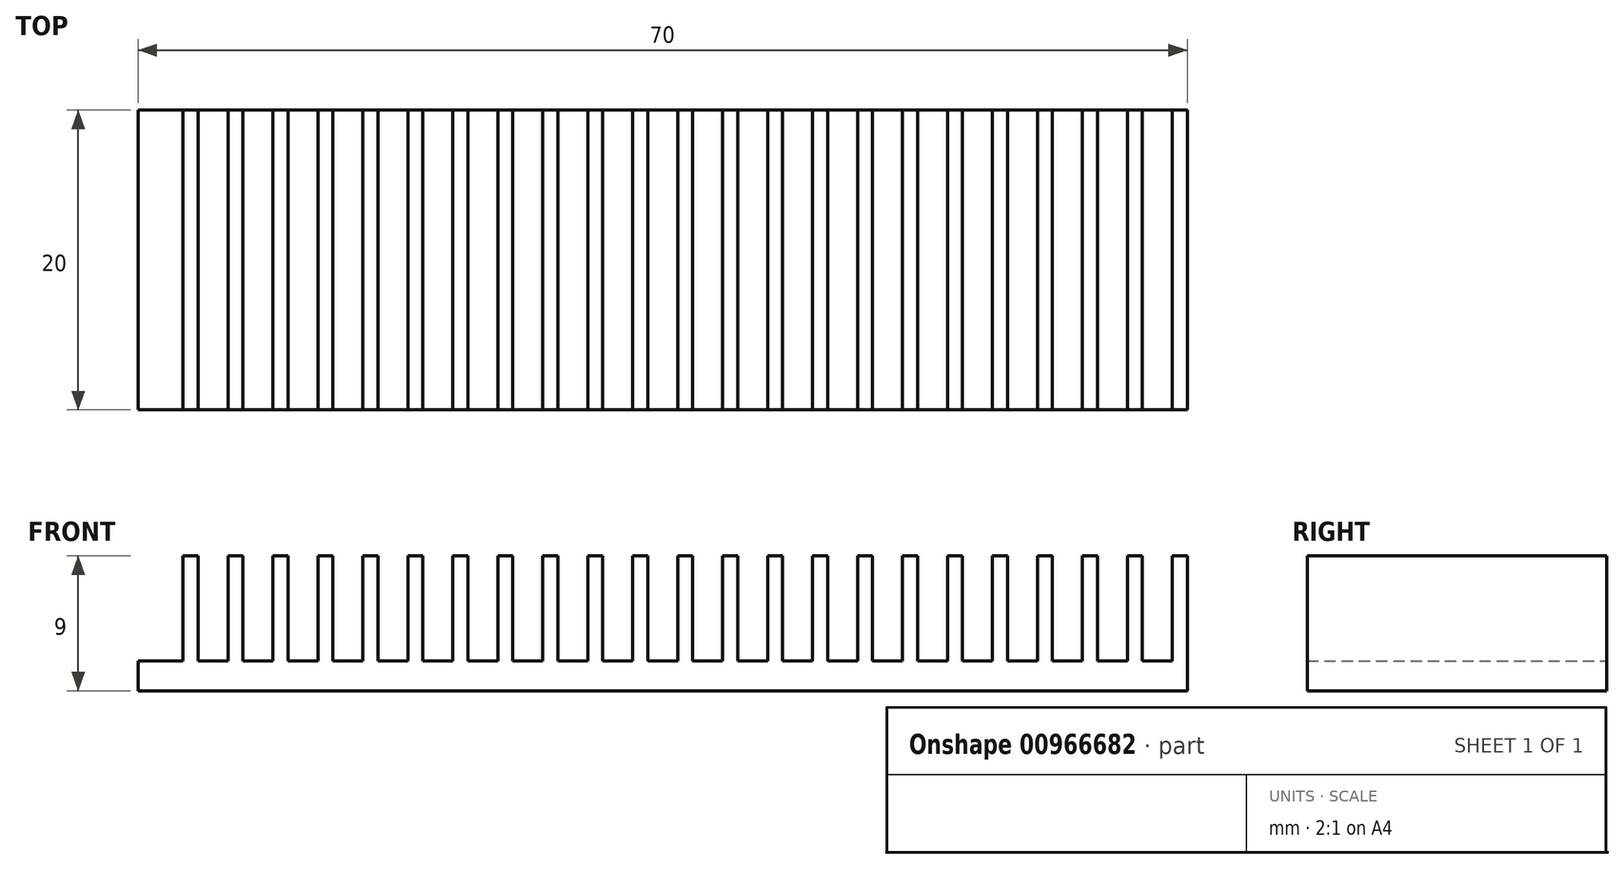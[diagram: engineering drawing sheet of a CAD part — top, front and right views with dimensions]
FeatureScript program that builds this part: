
annotation { "Feature Type Name" : "Feature", "Feature Type Description" : "" }
export const myFeature = defineFeature(function(context is Context, id is Id, definition is map)
    precondition{}
    {
        {
            var Q0;
            Q0=qCreatedBy(makeId("Front.planeOp"),FACE);
            var sketch = newSketch(context, id + "F0", { "sketchPlane" : qUnion([Q0])});
            skLineSegment(sketch, "E0.bottom", {"start": v(-37.94, 0) * mm, "end": v(32.06, 0) * mm});
            skLineSegment(sketch, "E0.top", {"start": v(-37.94, 2) * mm, "end": v(32.06, 2) * mm});
            skLineSegment(sketch, "E0.left", {"start": v(-37.94, 0) * mm, "end": v(-37.94, 2) * mm});
            skLineSegment(sketch, "E0.right", {"start": v(32.06, 0) * mm, "end": v(32.06, 2) * mm});
            skLineSegment(sketch, "E1.bottom", {"start": v(-37.94, 2) * mm, "end": v(-36.94, 2) * mm});
            skLineSegment(sketch, "E1.top", {"start": v(-37.94, 9) * mm, "end": v(-36.94, 9) * mm});
            skLineSegment(sketch, "E1.left", {"start": v(-37.94, 2) * mm, "end": v(-37.94, 9) * mm});
            skLineSegment(sketch, "E1.right", {"start": v(-36.94, 2) * mm, "end": v(-36.94, 9) * mm});
            skLineSegment(sketch, "E2.1.0.0", {"start": v(-34.94, 2) * mm, "end": v(-34.94, 9) * mm});
            skLineSegment(sketch, "E2.1.0.1", {"start": v(-34.94, 9) * mm, "end": v(-33.94, 9) * mm});
            skLineSegment(sketch, "E2.1.0.2", {"start": v(-33.94, 2) * mm, "end": v(-33.94, 9) * mm});
            skLineSegment(sketch, "E2.2.0.0", {"start": v(-31.94, 2) * mm, "end": v(-31.94, 9) * mm});
            skLineSegment(sketch, "E2.2.0.1", {"start": v(-31.94, 9) * mm, "end": v(-30.94, 9) * mm});
            skLineSegment(sketch, "E2.2.0.2", {"start": v(-30.94, 2) * mm, "end": v(-30.94, 9) * mm});
            skLineSegment(sketch, "E2.3.0.0", {"start": v(-28.94, 2) * mm, "end": v(-28.94, 9) * mm});
            skLineSegment(sketch, "E2.3.0.1", {"start": v(-28.94, 9) * mm, "end": v(-27.94, 9) * mm});
            skLineSegment(sketch, "E2.3.0.2", {"start": v(-27.94, 2) * mm, "end": v(-27.94, 9) * mm});
            skLineSegment(sketch, "E2.4.0.0", {"start": v(-25.94, 2) * mm, "end": v(-25.94, 9) * mm});
            skLineSegment(sketch, "E2.4.0.1", {"start": v(-25.94, 9) * mm, "end": v(-24.94, 9) * mm});
            skLineSegment(sketch, "E2.4.0.2", {"start": v(-24.94, 2) * mm, "end": v(-24.94, 9) * mm});
            skLineSegment(sketch, "E2.5.0.0", {"start": v(-22.94, 2) * mm, "end": v(-22.94, 9) * mm});
            skLineSegment(sketch, "E2.5.0.1", {"start": v(-22.94, 9) * mm, "end": v(-21.94, 9) * mm});
            skLineSegment(sketch, "E2.5.0.2", {"start": v(-21.94, 2) * mm, "end": v(-21.94, 9) * mm});
            skLineSegment(sketch, "E2.6.0.0", {"start": v(-19.94, 2) * mm, "end": v(-19.94, 9) * mm});
            skLineSegment(sketch, "E2.6.0.1", {"start": v(-19.94, 9) * mm, "end": v(-18.94, 9) * mm});
            skLineSegment(sketch, "E2.6.0.2", {"start": v(-18.94, 2) * mm, "end": v(-18.94, 9) * mm});
            skLineSegment(sketch, "E2.7.0.0", {"start": v(-16.94, 2) * mm, "end": v(-16.94, 9) * mm});
            skLineSegment(sketch, "E2.7.0.1", {"start": v(-16.94, 9) * mm, "end": v(-15.94, 9) * mm});
            skLineSegment(sketch, "E2.7.0.2", {"start": v(-15.94, 2) * mm, "end": v(-15.94, 9) * mm});
            skLineSegment(sketch, "E2.direction1", {"start": v(-37.94, 2) * mm, "end": v(-34.94, 2) * mm, "construction": true});
            skLineSegment(sketch, "E3.0.8.0", {"start": v(-13.94, 2) * mm, "end": v(-13.94, 9) * mm});
            skLineSegment(sketch, "E3.3.8.0", {"start": v(-13.94, 9) * mm, "end": v(-12.94, 9) * mm});
            skLineSegment(sketch, "E3.6.8.0", {"start": v(-12.94, 2) * mm, "end": v(-12.94, 9) * mm});
            skLineSegment(sketch, "E3.0.9.0", {"start": v(-10.94, 2) * mm, "end": v(-10.94, 9) * mm});
            skLineSegment(sketch, "E3.3.9.0", {"start": v(-10.94, 9) * mm, "end": v(-9.94, 9) * mm});
            skLineSegment(sketch, "E3.6.9.0", {"start": v(-9.94, 2) * mm, "end": v(-9.94, 9) * mm});
            skLineSegment(sketch, "E3.0.10.0", {"start": v(-7.94, 2) * mm, "end": v(-7.94, 9) * mm});
            skLineSegment(sketch, "E3.3.10.0", {"start": v(-7.94, 9) * mm, "end": v(-6.94, 9) * mm});
            skLineSegment(sketch, "E3.6.10.0", {"start": v(-6.94, 2) * mm, "end": v(-6.94, 9) * mm});
            skLineSegment(sketch, "E3.0.11.0", {"start": v(-4.94, 2) * mm, "end": v(-4.94, 9) * mm});
            skLineSegment(sketch, "E3.3.11.0", {"start": v(-4.94, 9) * mm, "end": v(-3.94, 9) * mm});
            skLineSegment(sketch, "E3.6.11.0", {"start": v(-3.94, 2) * mm, "end": v(-3.94, 9) * mm});
            skLineSegment(sketch, "E3.0.12.0", {"start": v(-1.94, 2) * mm, "end": v(-1.94, 9) * mm});
            skLineSegment(sketch, "E3.3.12.0", {"start": v(-1.94, 9) * mm, "end": v(-0.94, 9) * mm});
            skLineSegment(sketch, "E3.6.12.0", {"start": v(-0.94, 2) * mm, "end": v(-0.94, 9) * mm});
            skLineSegment(sketch, "E3.0.13.0", {"start": v(1.06, 2) * mm, "end": v(1.06, 9) * mm});
            skLineSegment(sketch, "E3.3.13.0", {"start": v(1.06, 9) * mm, "end": v(2.06, 9) * mm});
            skLineSegment(sketch, "E3.6.13.0", {"start": v(2.06, 2) * mm, "end": v(2.06, 9) * mm});
            skLineSegment(sketch, "E3.0.14.0", {"start": v(4.06, 2) * mm, "end": v(4.06, 9) * mm});
            skLineSegment(sketch, "E3.3.14.0", {"start": v(4.06, 9) * mm, "end": v(5.06, 9) * mm});
            skLineSegment(sketch, "E3.6.14.0", {"start": v(5.06, 2) * mm, "end": v(5.06, 9) * mm});
            skLineSegment(sketch, "E3.0.15.0", {"start": v(7.06, 2) * mm, "end": v(7.06, 9) * mm});
            skLineSegment(sketch, "E3.3.15.0", {"start": v(7.06, 9) * mm, "end": v(8.06, 9) * mm});
            skLineSegment(sketch, "E3.6.15.0", {"start": v(8.06, 2) * mm, "end": v(8.06, 9) * mm});
            skLineSegment(sketch, "E3.0.16.0", {"start": v(10.06, 2) * mm, "end": v(10.06, 9) * mm});
            skLineSegment(sketch, "E3.3.16.0", {"start": v(10.06, 9) * mm, "end": v(11.06, 9) * mm});
            skLineSegment(sketch, "E3.6.16.0", {"start": v(11.06, 2) * mm, "end": v(11.06, 9) * mm});
            skLineSegment(sketch, "E3.0.17.0", {"start": v(13.06, 2) * mm, "end": v(13.06, 9) * mm});
            skLineSegment(sketch, "E3.3.17.0", {"start": v(13.06, 9) * mm, "end": v(14.06, 9) * mm});
            skLineSegment(sketch, "E3.6.17.0", {"start": v(14.06, 2) * mm, "end": v(14.06, 9) * mm});
            skLineSegment(sketch, "E3.0.18.0", {"start": v(16.06, 2) * mm, "end": v(16.06, 9) * mm});
            skLineSegment(sketch, "E3.3.18.0", {"start": v(16.06, 9) * mm, "end": v(17.06, 9) * mm});
            skLineSegment(sketch, "E3.6.18.0", {"start": v(17.06, 2) * mm, "end": v(17.06, 9) * mm});
            skLineSegment(sketch, "E3.0.19.0", {"start": v(19.06, 2) * mm, "end": v(19.06, 9) * mm});
            skLineSegment(sketch, "E3.3.19.0", {"start": v(19.06, 9) * mm, "end": v(20.06, 9) * mm});
            skLineSegment(sketch, "E3.6.19.0", {"start": v(20.06, 2) * mm, "end": v(20.06, 9) * mm});
            skLineSegment(sketch, "E3.0.20.0", {"start": v(22.06, 2) * mm, "end": v(22.06, 9) * mm});
            skLineSegment(sketch, "E3.3.20.0", {"start": v(22.06, 9) * mm, "end": v(23.06, 9) * mm});
            skLineSegment(sketch, "E3.6.20.0", {"start": v(23.06, 2) * mm, "end": v(23.06, 9) * mm});
            skLineSegment(sketch, "E3.0.21.0", {"start": v(25.06, 2) * mm, "end": v(25.06, 9) * mm});
            skLineSegment(sketch, "E3.3.21.0", {"start": v(25.06, 9) * mm, "end": v(26.06, 9) * mm});
            skLineSegment(sketch, "E3.6.21.0", {"start": v(26.06, 2) * mm, "end": v(26.06, 9) * mm});
            skLineSegment(sketch, "E3.0.22.0", {"start": v(28.06, 2) * mm, "end": v(28.06, 9) * mm});
            skLineSegment(sketch, "E3.3.22.0", {"start": v(28.06, 9) * mm, "end": v(29.06, 9) * mm});
            skLineSegment(sketch, "E3.6.22.0", {"start": v(29.06, 2) * mm, "end": v(29.06, 9) * mm});
            skLineSegment(sketch, "E3.0.23.0", {"start": v(31.06, 2) * mm, "end": v(31.06, 9) * mm});
            skLineSegment(sketch, "E3.3.23.0", {"start": v(31.06, 9) * mm, "end": v(32.06, 9) * mm});
            skLineSegment(sketch, "E3.6.23.0", {"start": v(32.06, 2) * mm, "end": v(32.06, 9) * mm});
            skSolve(sketch);
        }
        {
            var Q0;
            Q0=makeQuery(id+"F0.imprint","IMPRINT",FACE,{"disambiguationData":[TD([[makeQuery(id+"F0.imprint","IMPRINT",EDGE,{"derivedFrom":sQuery(id+"F0.wireOp",EDGE,"E1.bottom")}),1.0]])]});
            var Q1;
            {var subQ2=sQuery(id+"F0.wireOp",EDGE,"E3.0.23.0");Q1=makeQuery(id+"F0.imprint","IMPRINT",FACE,{"disambiguationData":[TD([[makeQuery(id+"F0.imprint","IMPRINT",EDGE,{"derivedFrom":subQ2}),-1.0]])]});}
            var Q2;
            {var subQ0=sQuery(id+"F0.wireOp",EDGE,"E3.0.9.0");Q2=makeQuery(id+"F0.imprint","IMPRINT",FACE,{"disambiguationData":[TD([[makeQuery(id+"F0.imprint","IMPRINT",EDGE,{"derivedFrom":subQ0}),-1.0]])]});}
            var Q3;
            {var subQ0=sQuery(id+"F0.wireOp",EDGE,"E3.0.11.0");Q3=makeQuery(id+"F0.imprint","IMPRINT",FACE,{"disambiguationData":[TD([[makeQuery(id+"F0.imprint","IMPRINT",EDGE,{"derivedFrom":subQ0}),-1.0]])]});}
            var Q4;
            {var subQ0=sQuery(id+"F0.wireOp",EDGE,"E3.0.16.0");Q4=makeQuery(id+"F0.imprint","IMPRINT",FACE,{"disambiguationData":[TD([[makeQuery(id+"F0.imprint","IMPRINT",EDGE,{"derivedFrom":subQ0}),-1.0]])]});}
            var Q5;
            {var subQ0=sQuery(id+"F0.wireOp",EDGE,"E3.0.18.0");Q5=makeQuery(id+"F0.imprint","IMPRINT",FACE,{"disambiguationData":[TD([[makeQuery(id+"F0.imprint","IMPRINT",EDGE,{"derivedFrom":subQ0}),-1.0]])]});}
            var Q6;
            {var subQ0=sQuery(id+"F0.wireOp",EDGE,"E3.0.20.0");Q6=makeQuery(id+"F0.imprint","IMPRINT",FACE,{"disambiguationData":[TD([[makeQuery(id+"F0.imprint","IMPRINT",EDGE,{"derivedFrom":subQ0}),-1.0]])]});}
            var Q7;
            {var subQ0=sQuery(id+"F0.wireOp",EDGE,"E3.0.22.0");Q7=makeQuery(id+"F0.imprint","IMPRINT",FACE,{"disambiguationData":[TD([[makeQuery(id+"F0.imprint","IMPRINT",EDGE,{"derivedFrom":subQ0}),-1.0]])]});}
            var Q8;
            {var subQ0=sQuery(id+"F0.wireOp",EDGE,"E3.0.15.0");Q8=makeQuery(id+"F0.imprint","IMPRINT",FACE,{"disambiguationData":[TD([[makeQuery(id+"F0.imprint","IMPRINT",EDGE,{"derivedFrom":subQ0}),-1.0]])]});}
            var Q9;
            {var subQ0=sQuery(id+"F0.wireOp",EDGE,"E3.0.13.0");Q9=makeQuery(id+"F0.imprint","IMPRINT",FACE,{"disambiguationData":[TD([[makeQuery(id+"F0.imprint","IMPRINT",EDGE,{"derivedFrom":subQ0}),-1.0]])]});}
            var Q10;
            {var subQ0=sQuery(id+"F0.wireOp",EDGE,"E3.0.19.0");Q10=makeQuery(id+"F0.imprint","IMPRINT",FACE,{"disambiguationData":[TD([[makeQuery(id+"F0.imprint","IMPRINT",EDGE,{"derivedFrom":subQ0}),-1.0]])]});}
            var Q11;
            {var subQ0=sQuery(id+"F0.wireOp",EDGE,"E2.7.0.0");Q11=makeQuery(id+"F0.imprint","IMPRINT",FACE,{"disambiguationData":[TD([[makeQuery(id+"F0.imprint","IMPRINT",EDGE,{"derivedFrom":subQ0}),-1.0]])]});}
            var Q12;
            {var subQ0=sQuery(id+"F0.wireOp",EDGE,"E3.0.14.0");Q12=makeQuery(id+"F0.imprint","IMPRINT",FACE,{"disambiguationData":[TD([[makeQuery(id+"F0.imprint","IMPRINT",EDGE,{"derivedFrom":subQ0}),-1.0]])]});}
            var Q13;
            {var subQ0=sQuery(id+"F0.wireOp",EDGE,"E2.1.0.0");Q13=makeQuery(id+"F0.imprint","IMPRINT",FACE,{"disambiguationData":[TD([[makeQuery(id+"F0.imprint","IMPRINT",EDGE,{"derivedFrom":subQ0}),-1.0]])]});}
            var Q14;
            {var subQ0=sQuery(id+"F0.wireOp",EDGE,"E2.4.0.0");Q14=makeQuery(id+"F0.imprint","IMPRINT",FACE,{"disambiguationData":[TD([[makeQuery(id+"F0.imprint","IMPRINT",EDGE,{"derivedFrom":subQ0}),-1.0]])]});}
            var Q15;
            {var subQ0=sQuery(id+"F0.wireOp",EDGE,"E2.2.0.0");Q15=makeQuery(id+"F0.imprint","IMPRINT",FACE,{"disambiguationData":[TD([[makeQuery(id+"F0.imprint","IMPRINT",EDGE,{"derivedFrom":subQ0}),-1.0]])]});}
            var Q16;
            {var subQ0=sQuery(id+"F0.wireOp",EDGE,"E2.5.0.0");Q16=makeQuery(id+"F0.imprint","IMPRINT",FACE,{"disambiguationData":[TD([[makeQuery(id+"F0.imprint","IMPRINT",EDGE,{"derivedFrom":subQ0}),-1.0]])]});}
            var Q17;
            {var subQ0=sQuery(id+"F0.wireOp",EDGE,"E3.0.8.0");Q17=makeQuery(id+"F0.imprint","IMPRINT",FACE,{"disambiguationData":[TD([[makeQuery(id+"F0.imprint","IMPRINT",EDGE,{"derivedFrom":subQ0}),-1.0]])]});}
            var Q18;
            {var subQ0=sQuery(id+"F0.wireOp",EDGE,"E3.0.12.0");Q18=makeQuery(id+"F0.imprint","IMPRINT",FACE,{"disambiguationData":[TD([[makeQuery(id+"F0.imprint","IMPRINT",EDGE,{"derivedFrom":subQ0}),-1.0]])]});}
            var Q19;
            {var subQ0=sQuery(id+"F0.wireOp",EDGE,"E3.0.17.0");Q19=makeQuery(id+"F0.imprint","IMPRINT",FACE,{"disambiguationData":[TD([[makeQuery(id+"F0.imprint","IMPRINT",EDGE,{"derivedFrom":subQ0}),-1.0]])]});}
            var Q20;
            {var subQ0=sQuery(id+"F0.wireOp",EDGE,"E3.0.10.0");Q20=makeQuery(id+"F0.imprint","IMPRINT",FACE,{"disambiguationData":[TD([[makeQuery(id+"F0.imprint","IMPRINT",EDGE,{"derivedFrom":subQ0}),-1.0]])]});}
            var Q21;
            {var subQ0=sQuery(id+"F0.wireOp",EDGE,"E3.0.21.0");Q21=makeQuery(id+"F0.imprint","IMPRINT",FACE,{"disambiguationData":[TD([[makeQuery(id+"F0.imprint","IMPRINT",EDGE,{"derivedFrom":subQ0}),-1.0]])]});}
            var Q22;
            {var subQ0=sQuery(id+"F0.wireOp",EDGE,"E2.6.0.0");Q22=makeQuery(id+"F0.imprint","IMPRINT",FACE,{"disambiguationData":[TD([[makeQuery(id+"F0.imprint","IMPRINT",EDGE,{"derivedFrom":subQ0}),-1.0]])]});}
            var Q23;
            {var subQ0=sQuery(id+"F0.wireOp",EDGE,"E2.3.0.0");Q23=makeQuery(id+"F0.imprint","IMPRINT",FACE,{"disambiguationData":[TD([[makeQuery(id+"F0.imprint","IMPRINT",EDGE,{"derivedFrom":subQ0}),-1.0]])]});}
            var Q24;
            Q24=makeQuery(id+"F0.imprint","IMPRINT",FACE,{"disambiguationData":[TD([[makeQuery(id+"F0.imprint","IMPRINT",EDGE,{"derivedFrom":sQuery(id+"F0.wireOp",EDGE,"E0.bottom")}),1.0]])]});
            extrude(context, id + "F1", {"entities" : qUnion([Q0, Q1, Q2, Q3, Q4, Q5, Q6, Q7, Q8, Q9, Q10, Q11, Q12, Q13, Q14, Q15, Q16, Q17, Q18, Q19, Q20, Q21, Q22, Q23, Q24]), "depth" : 20 * mm, "offsetDistance" : 25.4 * mm});
        }
    });
